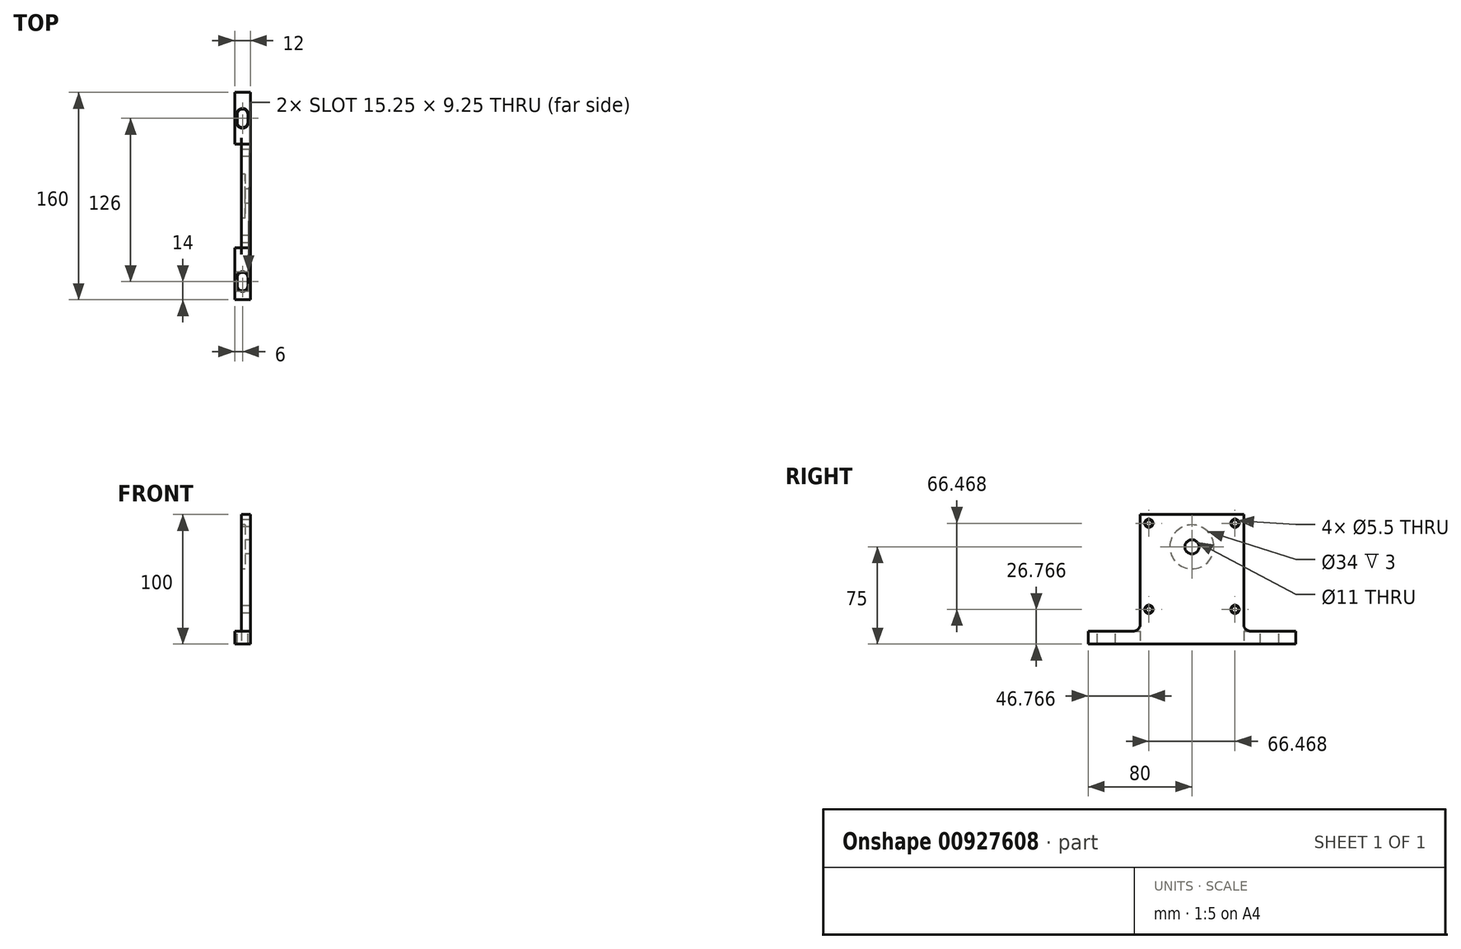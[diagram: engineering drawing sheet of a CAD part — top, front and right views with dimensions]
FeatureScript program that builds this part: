
annotation { "Feature Type Name" : "Feature", "Feature Type Description" : "" }
export const myFeature = defineFeature(function(context is Context, id is Id, definition is map)
    precondition{}
    {
        {
            var Q0;
            Q0=qCreatedBy(makeId("Right.planeOp"),FACE);
            var sketch = newSketch(context, id + "F0", { "sketchPlane" : qUnion([Q0])});
            skLineSegment(sketch, "E0", {"start": v(0, 139.68) * mm, "end": v(0, -17.58) * mm, "construction": true});
            skLineSegment(sketch, "E1", {"start": v(0, 0) * mm, "end": v(80, 0) * mm});
            skLineSegment(sketch, "E2", {"start": v(80, 0) * mm, "end": v(80, 10) * mm});
            skLineSegment(sketch, "E3", {"start": v(80, 10) * mm, "end": v(40, 10) * mm});
            skLineSegment(sketch, "E4", {"start": v(40, 10) * mm, "end": v(40, 100) * mm});
            skLineSegment(sketch, "E5", {"start": v(40, 100) * mm, "end": v(0, 100) * mm});
            skLineSegment(sketch, "E6.MirrorCS", {"start": v(-40, 100) * mm, "end": v(0, 100) * mm});
            skLineSegment(sketch, "E7.MirrorCS", {"start": v(-40, 10) * mm, "end": v(-40, 100) * mm});
            skLineSegment(sketch, "E8.MirrorCS", {"start": v(-80, 10) * mm, "end": v(-40, 10) * mm});
            skLineSegment(sketch, "E9.MirrorCS", {"start": v(-80, 0) * mm, "end": v(-80, 10) * mm});
            skLineSegment(sketch, "E10.MirrorCS", {"start": v(0, 0) * mm, "end": v(-80, 0) * mm});
            skPoint(sketch, "E11.startSnap0", {"position": v(-40, 55) * mm});
            skCircle(sketch, "E12", {"center": v(33.23, 93.23) * mm, "radius": 2.75 * mm});
            skLineSegment(sketch, "E13", {"start": v(-40, 100) * mm, "end": v(40, 20) * mm, "construction": true});
            skLineSegment(sketch, "E14", {"start": v(40, 100) * mm, "end": v(-40, 20) * mm, "construction": true});
            skPoint(sketch, "E15", {"position": v(0, 60) * mm});
            skLineSegment(sketch, "E16", {"start": v(-55.97, 60) * mm, "end": v(54.6, 60) * mm, "construction": true});
            skCircle(sketch, "E17.MirrorC", {"center": v(33.23, 26.77) * mm, "radius": 2.75 * mm});
            skCircle(sketch, "E18.MirrorC", {"center": v(-33.23, 93.23) * mm, "radius": 2.75 * mm});
            skCircle(sketch, "E19.MirrorC", {"center": v(-33.23, 26.77) * mm, "radius": 2.75 * mm});
            skCircle(sketch, "E20", {"center": v(0, 60) * mm, "radius": 47 * mm, "construction": true});
            skSolve(sketch);
        }
        {
            var Q0;
            Q0=makeQuery(id+"F0.imprint","IMPRINT",FACE,{"disambiguationData":[TD([[makeQuery(id+"F0.imprint","IMPRINT",EDGE,{"derivedFrom":sQuery(id+"F0.wireOp",EDGE,"E1")}),1.0]])]});
            extrude(context, id + "F1", {"entities" : qUnion([Q0]), "depth" : 12 * mm, "offsetDistance" : 25 * mm});
        }
        {
            var Q0;
            Q0=makeQuery(id+"F1.opExtrude","SWEPT_FACE",FACE,{"disambiguationData":[OSD([sQuery(id+"F0.wireOp",EDGE,"E3")])]});
            var sketch = newSketch(context, id + "F2", { "sketchPlane" : qUnion([Q0])});
            skLineSegment(sketch, "E21", {"start": v(-16.7, 60) * mm, "end": v(59.99, 60) * mm, "construction": true});
            skPoint(sketch, "E21.startSnap0", {"position": v(0, 60) * mm});
            skLineSegment(sketch, "E22", {"start": v(-8.13, -66) * mm, "end": v(54.79, -66) * mm, "construction": true});
            skLineSegment(sketch, "E23", {"start": v(6, 85.77) * mm, "end": v(6, -87.81) * mm, "construction": true});
            skPoint(sketch, "E23.startSnap0", {"position": v(6, 80) * mm});
            skArc(sketch, "E24", {"start": v(10.13, 63) * mm, "mid": v(6, 67.13) * mm, "end": v(1.88, 63) * mm});
            skArc(sketch, "E25", {"start": v(1.88, 57) * mm, "mid": v(6, 52.88) * mm, "end": v(10.13, 57) * mm});
            skLineSegment(sketch, "E26", {"start": v(1.88, 63) * mm, "end": v(1.88, 57) * mm});
            skLineSegment(sketch, "E27", {"start": v(10.13, 63) * mm, "end": v(10.13, 57) * mm});
            skArc(sketch, "E28", {"start": v(10.13, -63) * mm, "mid": v(6, -58.88) * mm, "end": v(1.88, -63) * mm});
            skArc(sketch, "E29", {"start": v(1.88, -69) * mm, "mid": v(6, -73.13) * mm, "end": v(10.13, -69) * mm});
            skLineSegment(sketch, "E30", {"start": v(1.88, -63) * mm, "end": v(1.88, -69) * mm});
            skLineSegment(sketch, "E31", {"start": v(10.13, -63) * mm, "end": v(10.13, -69) * mm});
            skSolve(sketch);
        }
        {
            var Q0;
            Q0 = qSketchRegion(id + "F2", true);
            extrude(context, id + "F3", {"entities" : qUnion([Q0]), "operationType" : NewBodyOperationType.REMOVE, "endBound" : BoundingType.THROUGH_ALL, "oppositeDirection" : true, "depth" : 25 * mm, "offsetDistance" : 25 * mm});
        }
        {
            var Q0;
            Q0=makeQuery(id+"F3.boolean.opBoolean","COPY",FACE,{"derivedFrom":makeQuery(id+"F3.opExtrude","SWEPT_FACE",FACE,{"disambiguationData":[OSD([sQuery(id+"F2.wireOp",EDGE,"E25")])]})});
            var Q1;
            Q1=makeQuery(id+"F3.boolean.opBoolean","COPY",FACE,{"derivedFrom":makeQuery(id+"F3.opExtrude","SWEPT_FACE",FACE,{"disambiguationData":[OSD([sQuery(id+"F2.wireOp",EDGE,"E28")])]})});
            chamfer(context, id + "F4", {"entities" : qUnion([Q0, Q1]), "width" : 0.5 * mm, "tangentPropagation" : true});
        }
        {
            var Q0;
            Q0=makeQuery(id+"F1.opExtrude","SWEPT_FACE",FACE,{"disambiguationData":[OSD([sQuery(id+"F0.wireOp",EDGE,"E18.MirrorC")])]});
            var Q1;
            Q1=makeQuery(id+"F1.opExtrude","SWEPT_FACE",FACE,{"disambiguationData":[OSD([sQuery(id+"F0.wireOp",EDGE,"E12")])]});
            var Q2;
            Q2=makeQuery(id+"F1.opExtrude","SWEPT_FACE",FACE,{"disambiguationData":[OSD([sQuery(id+"F0.wireOp",EDGE,"E19.MirrorC")])]});
            var Q3;
            Q3=makeQuery(id+"F1.opExtrude","SWEPT_FACE",FACE,{"disambiguationData":[OSD([sQuery(id+"F0.wireOp",EDGE,"E17.MirrorC")])]});
            chamfer(context, id + "F5", {"entities" : qUnion([Q0, Q1, Q2, Q3]), "width" : 0.5 * mm, "tangentPropagation" : true});
        }
        {
            var Q0;
            Q0=makeQuery(id+"F1.opExtrude","CAP_FACE",FACE,{"disambiguationData":[OSD([sQuery(id+"F0.wireOp",EDGE,"E1"),sQuery(id+"F0.wireOp",EDGE,"E2"),sQuery(id+"F0.wireOp",EDGE,"E3"),sQuery(id+"F0.wireOp",EDGE,"E4"),sQuery(id+"F0.wireOp",EDGE,"E5"),sQuery(id+"F0.wireOp",EDGE,"E6.MirrorCS"),sQuery(id+"F0.wireOp",EDGE,"E7.MirrorCS"),sQuery(id+"F0.wireOp",EDGE,"E8.MirrorCS"),sQuery(id+"F0.wireOp",EDGE,"E9.MirrorCS"),sQuery(id+"F0.wireOp",EDGE,"E10.MirrorCS"),sQuery(id+"F0.wireOp",EDGE,"E12"),sQuery(id+"F0.wireOp",EDGE,"E17.MirrorC"),sQuery(id+"F0.wireOp",EDGE,"E18.MirrorC"),sQuery(id+"F0.wireOp",EDGE,"E19.MirrorC"),sQuery(id+"F0.wireOp",EDGE,"EK6SEvZH-EAvm-7VDK-wsuZ-reFzIUpTzpa4")])],"isStart":true});
            var sketch = newSketch(context, id + "F6", { "sketchPlane" : qUnion([Q0])});
            skLineSegment(sketch, "E32.bottom", {"start": v(-40, 100) * mm, "end": v(40, 100) * mm});
            skLineSegment(sketch, "E32.top", {"start": v(-40, -4) * mm, "end": v(40, -4) * mm});
            skLineSegment(sketch, "E32.left", {"start": v(-40, 100) * mm, "end": v(-40, -4) * mm});
            skLineSegment(sketch, "E32.right", {"start": v(40, 100) * mm, "end": v(40, -4) * mm});
            skSolve(sketch);
        }
        {
            var Q0;
            Q0 = qSketchRegion(id + "F6", true);
            extrude(context, id + "F7", {"entities" : qUnion([Q0]), "operationType" : NewBodyOperationType.REMOVE, "oppositeDirection" : true, "depth" : 5 * mm, "offsetDistance" : 25 * mm});
        }
        {
            var Q0;
            Q0=makeQuery(id+"F7.boolean.opBoolean","COPY",FACE,{"derivedFrom":makeQuery(id+"F7.opExtrude","CAP_FACE",FACE,{"disambiguationData":[OSD([sQuery(id+"F6.wireOp",EDGE,"E32.bottom"),sQuery(id+"F6.wireOp",EDGE,"E32.top"),sQuery(id+"F6.wireOp",EDGE,"E32.left"),sQuery(id+"F6.wireOp",EDGE,"E32.right")])],"isStart":false})});
            var sketch = newSketch(context, id + "F8", { "sketchPlane" : qUnion([Q0])});
            skLineSegment(sketch, "E33", {"start": v(0, 126.64) * mm, "end": v(0, 5.68) * mm, "construction": true});
            skPoint(sketch, "E33.startSnap0", {"position": v(0, 100) * mm});
            skPoint(sketch, "E34", {"position": v(-33.23, 93.23) * mm});
            skCircle(sketch, "E35", {"center": v(0, 75) * mm, "radius": 17 * mm});
            skLineSegment(sketch, "E36", {"start": v(-33.23, 93.23) * mm, "end": v(33.23, 26.77) * mm, "construction": true});
            skLineSegment(sketch, "E37", {"start": v(33.23, 93.23) * mm, "end": v(-33.23, 26.77) * mm, "construction": true});
            skPoint(sketch, "E38", {"position": v(0, 60) * mm});
            skCircle(sketch, "E39", {"center": v(0, 75) * mm, "radius": 5.5 * mm});
            skSolve(sketch);
        }
        {
            var Q0;
            Q0 = qSketchRegion(id + "F8", true);
            extrude(context, id + "F9", {"entities" : qUnion([Q0]), "operationType" : NewBodyOperationType.REMOVE, "oppositeDirection" : true, "depth" : 3 * mm, "offsetDistance" : 25 * mm});
        }
        {
            var Q0;
            {var subQ0=sQuery(id+"F0.wireOp",EDGE,"E3");var subQ1=sQuery(id+"F0.wireOp",EDGE,"E4");Q0=makeQuery(id+"F7.boolean.opBoolean","SPLIT",EDGE,{"disambiguationData":[topologyDisambiguationEdgeConnected([makeQuery(id+"F1.opExtrude","SWEPT_FACE",FACE,{"disambiguationData":[OSD([subQ1])]})])],"derivedFrom":makeQuery(id+"F1.opExtrude","SWEPT_EDGE",EDGE,{"disambiguationData":[OSD([subQ0,subQ1])]})});}
            var Q1;
            {var subQ0=sQuery(id+"F0.wireOp",EDGE,"E7.MirrorCS");var subQ1=sQuery(id+"F0.wireOp",EDGE,"E8.MirrorCS");Q1=makeQuery(id+"F7.boolean.opBoolean","SPLIT",EDGE,{"disambiguationData":[topologyDisambiguationEdgeConnected([makeQuery(id+"F1.opExtrude","SWEPT_FACE",FACE,{"disambiguationData":[OSD([subQ0])]})])],"derivedFrom":makeQuery(id+"F1.opExtrude","SWEPT_EDGE",EDGE,{"disambiguationData":[OSD([subQ0,subQ1])]})});}
            fillet(context, id + "F10", {"entities" : qUnion([Q0, Q1]), "radius" : 5 * mm, "tangentPropagation" : true, "allowEdgeOverflow" : false});
        }
        {
            var Q0;
            Q0=makeQuery(id+"F9.boolean.opBoolean","SPLIT",FACE,{"disambiguationData":[TD([makeQuery(id+"F9.opExtrude","SWEPT_FACE",FACE,{"disambiguationData":[OSD([sQuery(id+"F8.wireOp",EDGE,"E39")])]})])],"derivedFrom":makeQuery(id+"F7.boolean.opBoolean","COPY",FACE,{"derivedFrom":makeQuery(id+"F7.opExtrude","CAP_FACE",FACE,{"disambiguationData":[OSD([sQuery(id+"F6.wireOp",EDGE,"E32.bottom"),sQuery(id+"F6.wireOp",EDGE,"E32.top"),sQuery(id+"F6.wireOp",EDGE,"E32.left"),sQuery(id+"F6.wireOp",EDGE,"E32.right")])],"isStart":false})})});
            extrude(context, id + "F11", {"entities" : qUnion([Q0]), "operationType" : NewBodyOperationType.REMOVE, "endBound" : BoundingType.THROUGH_ALL, "oppositeDirection" : true, "depth" : 25 * mm, "offsetDistance" : 25 * mm});
        }
    });
